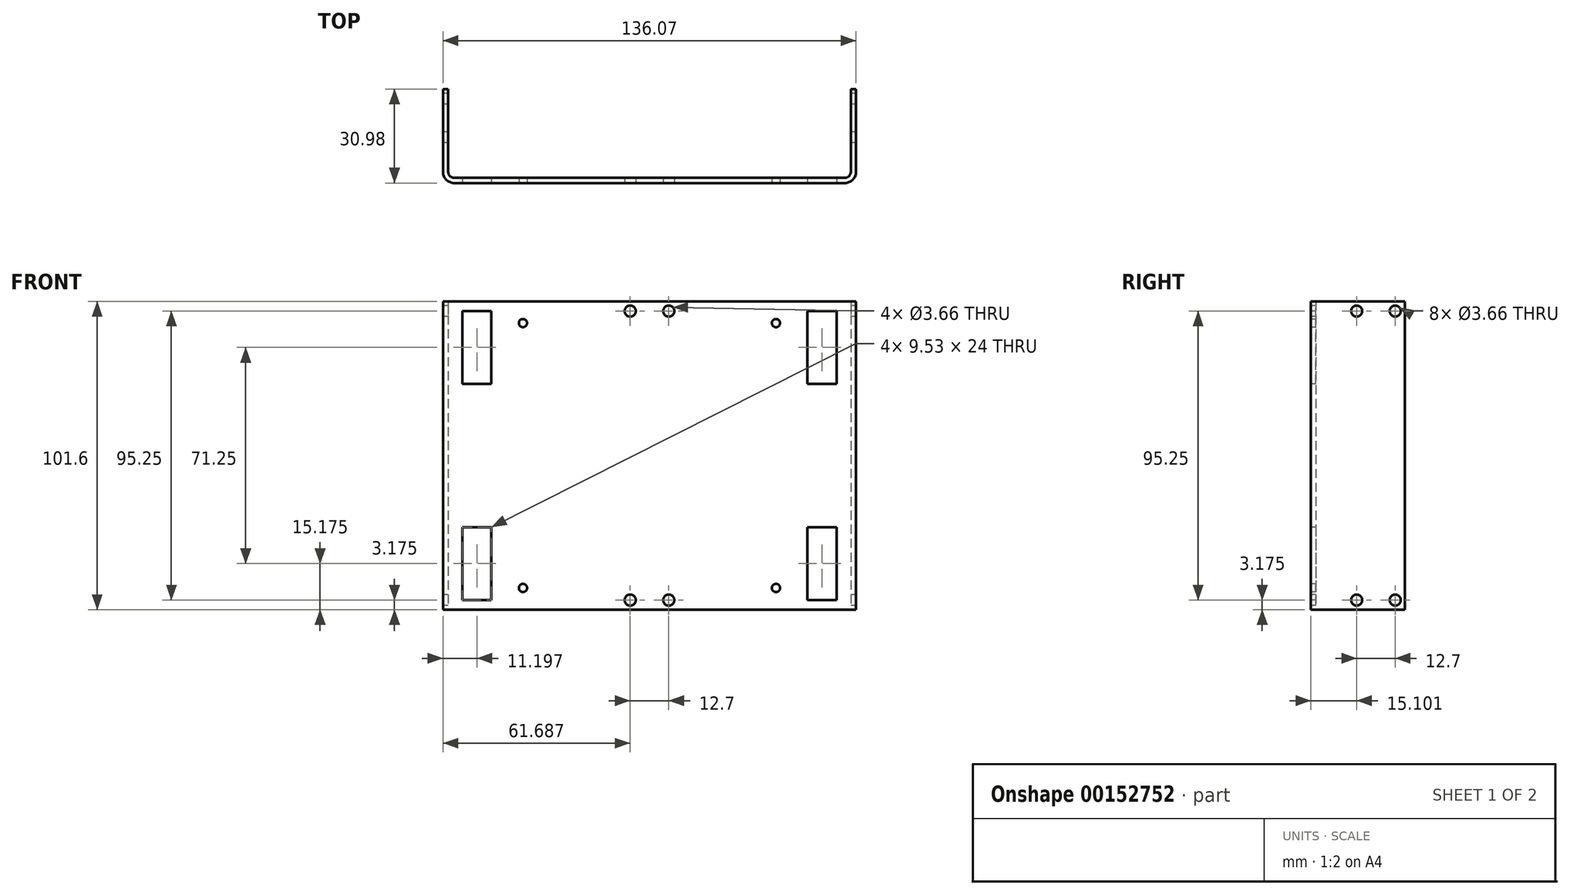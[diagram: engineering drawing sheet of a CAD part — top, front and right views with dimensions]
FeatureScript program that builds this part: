
annotation { "Feature Type Name" : "Feature", "Feature Type Description" : "" }
export const myFeature = defineFeature(function(context is Context, id is Id, definition is map)
    precondition{}
    {
        {
            var Q0;
            Q0=qCreatedBy(makeId("Top.planeOp"),FACE);
            var sketch = newSketch(context, id + "F0", { "sketchPlane" : qUnion([Q0])});
            skLineSegment(sketch, "E0.bottom", {"start": v(0, 0) * mm, "end": v(-132.65, 0) * mm});
            skLineSegment(sketch, "E0.top", {"start": v(1.7, -1.7) * mm, "end": v(-134.36, -1.7) * mm});
            skLineSegment(sketch, "E1.top", {"start": v(-132.65, 29.27) * mm, "end": v(-134.36, 29.27) * mm});
            skLineSegment(sketch, "E1.left", {"start": v(-132.65, 0) * mm, "end": v(-132.65, 29.27) * mm});
            skLineSegment(sketch, "E1.right", {"start": v(-134.36, -1.7) * mm, "end": v(-134.36, 29.27) * mm});
            skLineSegment(sketch, "E2.top", {"start": v(0, 29.27) * mm, "end": v(1.7, 29.27) * mm});
            skLineSegment(sketch, "E2.left", {"start": v(0, 0) * mm, "end": v(0, 29.27) * mm});
            skLineSegment(sketch, "E2.right", {"start": v(1.7, -1.7) * mm, "end": v(1.7, 29.27) * mm});
            skLineSegment(sketch, "E3", {"start": v(-66.32, 0) * mm, "end": v(-66.32, -1.7) * mm, "construction": true});
            skSolve(sketch);
        }
        {
            var Q0;
            Q0=qSketchRegion(id+"F0",true);
            extrude(context, id + "F1", {"entities" : qUnion([Q0]), "depth" : 101.6 * mm});
        }
        {
            var Q0;
            Q0=makeQuery(id+"FBItojHO8814Spz_1.opExtrude","CAP_EDGE",EDGE,{"disambiguationData":[OSD([sQuery(id+"FUP6qXxoG76JSYb_1.wireOp",EDGE,"THhbgtQy-TwxC-mwnz-G1VQ-umnQbeZaK48w.top")])],"isStart":true});
            var Q1;
            Q1=makeQuery(id+"FcdIcV9w6YY9zah_1.opExtrude","CAP_EDGE",EDGE,{"disambiguationData":[OSD([sQuery(id+"FU7sgaIbCbRhSfr_1.wireOp",EDGE,"F29Sxc5V-O2cl-wjtz-gx5o-reTTBG7m1pNU.top")])],"isStart":true});
            var Q2;
            Q2=makeQuery(id+"FxyfTe7Czhdyx7B_1.opExtrude","CAP_EDGE",EDGE,{"disambiguationData":[OSD([sQuery(id+"FSFcS7Rq7llt4xF_1.wireOp",EDGE,"t1tKkxU0-9nQq-L00X-xvmB-zDJKT8Ek5K4t.top")])],"isStart":true});
            var Q3;
            Q3=makeQuery(id+"FxyfTe7Czhdyx7B_1.opExtrude","CAP_EDGE",EDGE,{"disambiguationData":[OSD([sQuery(id+"FSFcS7Rq7llt4xF_1.wireOp",EDGE,"hRkMf9XR-YJFt-15pq-nWkK-FIu6sRtvibO9.top")])],"isStart":true});
            var Q4;
            Q4=makeQuery(id+"FcdIcV9w6YY9zah_1.opExtrude","CAP_EDGE",EDGE,{"disambiguationData":[OSD([sQuery(id+"FU7sgaIbCbRhSfr_1.wireOp",EDGE,"yv2bQU74-Eht6-uYuo-WBF2-3C4kyuaz0slr.top")])],"isStart":true});
            var Q5;
            Q5=makeQuery(id+"FBItojHO8814Spz_1.opExtrude","CAP_EDGE",EDGE,{"disambiguationData":[OSD([sQuery(id+"FUP6qXxoG76JSYb_1.wireOp",EDGE,"IUdUpv5F-JSBg-2lHB-rE6Q-IiAhZBjA2grY.top")])],"isStart":true});
            var Q6;
            Q6=makeQuery(id+"F1.opExtrude","SWEPT_EDGE",EDGE,{"disambiguationData":[OSD([sQuery(id+"F0.wireOp",EDGE,"E0.bottom"),sQuery(id+"F0.wireOp",EDGE,"E2.left")])]});
            var Q7;
            Q7=makeQuery(id+"F1.opExtrude","SWEPT_EDGE",EDGE,{"disambiguationData":[OSD([sQuery(id+"F0.wireOp",EDGE,"E0.bottom"),sQuery(id+"F0.wireOp",EDGE,"E1.left")])]});
            fillet(context, id + "F2", {"entities" : qUnion([Q0, Q1, Q2, Q3, Q4, Q5, Q6, Q7]), "radius" : 1.98 * mm, "tangentPropagation" : true, "allowEdgeOverflow" : false});
        }
        {
            var Q0;
            Q0=makeQuery(id+"F1.opExtrude","SWEPT_EDGE",EDGE,{"disambiguationData":[OSD([sQuery(id+"F0.wireOp",EDGE,"E0.top"),sQuery(id+"F0.wireOp",EDGE,"E1.right")])]});
            var Q1;
            Q1=makeQuery(id+"F1.opExtrude","SWEPT_EDGE",EDGE,{"disambiguationData":[OSD([sQuery(id+"F0.wireOp",EDGE,"E0.top"),sQuery(id+"F0.wireOp",EDGE,"E2.right")])]});
            fillet(context, id + "F3", {"entities" : qUnion([Q0, Q1]), "radius" : 3.7 * mm, "tangentPropagation" : true, "allowEdgeOverflow" : false});
        }
        {
            var Q0;
            Q0=makeQuery(id+"F2kHonbXZaQoFrR_1.boolean.opBoolean","MERGE",FACE,{"derivedFrom":[makeQuery(id+"FkwQQH4eT4IjhdK_1.boolean.opBoolean","MERGE",FACE,{"derivedFrom":[makeQuery(id+"F1.opExtrude","SWEPT_FACE",FACE,{"disambiguationData":[OSD([sQuery(id+"F0.wireOp",EDGE,"E0.top")])]}),makeQuery(id+"FkwQQH4eT4IjhdK_1.opExtrude","SWEPT_FACE",FACE,{"disambiguationData":[OSD([sQuery(id+"FvDFSbhwMPyTNrQ_1.wireOp",EDGE,"223FG13h-YrEq-unoX-9EOi-DwKLLmwbrteD.top")])]})]}),makeQuery(id+"F2kHonbXZaQoFrR_1.opExtrude","SWEPT_FACE",FACE,{"disambiguationData":[OSD([sQuery(id+"FsAbJG8AZOSwdHE_1.wireOp",EDGE,"WRaIy3id-o2EU-qHqw-IwdC-eHQZRSiK4KpF.bottom")])]})]});
            var sketch = newSketch(context, id + "F4", { "sketchPlane" : qUnion([Q0])});
            skLineSegment(sketch, "E4.bottom", {"start": v(-4.72, 3.18) * mm, "end": v(-14.25, 3.18) * mm});
            skLineSegment(sketch, "E4.top", {"start": v(-4.72, 27.18) * mm, "end": v(-14.25, 27.18) * mm});
            skLineSegment(sketch, "E4.left", {"start": v(-4.72, 3.18) * mm, "end": v(-4.72, 27.18) * mm});
            skLineSegment(sketch, "E4.right", {"start": v(-14.25, 3.18) * mm, "end": v(-14.25, 27.18) * mm});
            skLineSegment(sketch, "E5.bottom", {"start": v(-127.93, 3.18) * mm, "end": v(-118.4, 3.18) * mm});
            skLineSegment(sketch, "E5.top", {"start": v(-127.93, 27.18) * mm, "end": v(-118.4, 27.18) * mm});
            skLineSegment(sketch, "E5.left", {"start": v(-127.93, 3.18) * mm, "end": v(-127.93, 27.18) * mm});
            skLineSegment(sketch, "E5.right", {"start": v(-118.4, 3.18) * mm, "end": v(-118.4, 27.18) * mm});
            skLineSegment(sketch, "E6.bottom", {"start": v(-127.93, 98.43) * mm, "end": v(-118.4, 98.43) * mm});
            skLineSegment(sketch, "E6.top", {"start": v(-127.93, 74.42) * mm, "end": v(-118.4, 74.42) * mm});
            skLineSegment(sketch, "E6.left", {"start": v(-127.93, 98.43) * mm, "end": v(-127.93, 74.43) * mm});
            skLineSegment(sketch, "E6.right", {"start": v(-118.4, 98.43) * mm, "end": v(-118.4, 74.43) * mm});
            skLineSegment(sketch, "E7.bottom", {"start": v(-4.72, 98.43) * mm, "end": v(-14.25, 98.43) * mm});
            skLineSegment(sketch, "E7.top", {"start": v(-4.72, 74.42) * mm, "end": v(-14.25, 74.42) * mm});
            skLineSegment(sketch, "E7.left", {"start": v(-4.72, 98.43) * mm, "end": v(-4.72, 74.43) * mm});
            skLineSegment(sketch, "E7.right", {"start": v(-14.25, 98.43) * mm, "end": v(-14.25, 74.43) * mm});
            skLineSegment(sketch, "E8", {"start": v(-66.32, 0) * mm, "end": v(-66.32, 101.6) * mm, "construction": true});
            skLineSegment(sketch, "E9.bottom", {"start": v(-14.25, 27.18) * mm, "end": v(-118.4, 27.18) * mm, "construction": true});
            skLineSegment(sketch, "E9.top", {"start": v(-14.25, 74.42) * mm, "end": v(-118.4, 74.42) * mm, "construction": true});
            skLineSegment(sketch, "E9.left", {"start": v(-14.25, 27.18) * mm, "end": v(-14.25, 74.43) * mm, "construction": true});
            skLineSegment(sketch, "E9.right", {"start": v(-118.4, 27.18) * mm, "end": v(-118.4, 74.43) * mm, "construction": true});
            skPoint(sketch, "E9.middle", {"position": v(-66.32, 50.8) * mm});
            skLineSegment(sketch, "E10", {"start": v(-9.48, 27.18) * mm, "end": v(-9.48, 50.8) * mm, "construction": true});
            skLineSegment(sketch, "E11", {"start": v(-9.48, 50.8) * mm, "end": v(-1.98, 50.8) * mm, "construction": true});
            skLineSegment(sketch, "E12", {"start": v(-9.48, 3.18) * mm, "end": v(-9.48, 0) * mm, "construction": true});
            skLineSegment(sketch, "E13.bottom", {"start": v(-24.65, 7.14) * mm, "end": v(-108, 7.14) * mm, "construction": true});
            skLineSegment(sketch, "E13.top", {"start": v(-24.65, 94.46) * mm, "end": v(-108, 94.46) * mm, "construction": true});
            skLineSegment(sketch, "E13.left", {"start": v(-24.65, 7.14) * mm, "end": v(-24.65, 94.46) * mm, "construction": true});
            skLineSegment(sketch, "E13.right", {"start": v(-108, 7.14) * mm, "end": v(-108, 94.46) * mm, "construction": true});
            skLineSegment(sketch, "E14", {"start": v(-24.65, 7.14) * mm, "end": v(-24.65, 3.18) * mm, "construction": true});
            skLineSegment(sketch, "E15", {"start": v(-24.65, 3.18) * mm, "end": v(-14.25, 3.18) * mm, "construction": true});
            skCircle(sketch, "E16", {"center": v(-24.65, 7.14) * mm, "radius": 1.35 * mm});
            skCircle(sketch, "E17", {"center": v(-108, 7.14) * mm, "radius": 1.35 * mm});
            skCircle(sketch, "E18", {"center": v(-108, 94.46) * mm, "radius": 1.35 * mm});
            skCircle(sketch, "E19", {"center": v(-24.65, 94.46) * mm, "radius": 1.35 * mm});
            skPoint(sketch, "E20", {"position": v(-123.16, 3.18) * mm});
            skLineSegment(sketch, "E21.bottom", {"start": v(-59.97, 3.18) * mm, "end": v(-72.67, 3.18) * mm, "construction": true});
            skLineSegment(sketch, "E21.top", {"start": v(-59.97, 98.43) * mm, "end": v(-72.67, 98.43) * mm, "construction": true});
            skLineSegment(sketch, "E21.left", {"start": v(-59.97, 3.17) * mm, "end": v(-59.97, 98.43) * mm, "construction": true});
            skLineSegment(sketch, "E21.right", {"start": v(-72.67, 3.17) * mm, "end": v(-72.67, 98.43) * mm, "construction": true});
            skCircle(sketch, "E22", {"center": v(-59.97, 3.18) * mm, "radius": 1.83 * mm});
            skCircle(sketch, "E23", {"center": v(-72.67, 3.18) * mm, "radius": 1.83 * mm});
            skCircle(sketch, "E24", {"center": v(-59.97, 98.43) * mm, "radius": 1.83 * mm});
            skCircle(sketch, "E25", {"center": v(-72.67, 98.43) * mm, "radius": 1.83 * mm});
            skSolve(sketch);
        }
        {
            var Q0;
            Q0=qSketchRegion(id+"F4",true);
            var Q1;
            Q1=makeQuery(id+"F2kHonbXZaQoFrR_1.boolean.opBoolean","MERGE",FACE,{"derivedFrom":[makeQuery(id+"FkwQQH4eT4IjhdK_1.boolean.opBoolean","MERGE",FACE,{"derivedFrom":[makeQuery(id+"F1.opExtrude","SWEPT_FACE",FACE,{"disambiguationData":[OSD([sQuery(id+"F0.wireOp",EDGE,"E0.bottom")])]}),makeQuery(id+"FkwQQH4eT4IjhdK_1.opExtrude","SWEPT_FACE",FACE,{"disambiguationData":[OSD([sQuery(id+"FvDFSbhwMPyTNrQ_1.wireOp",EDGE,"223FG13h-YrEq-unoX-9EOi-DwKLLmwbrteD.bottom")])]})]}),makeQuery(id+"F2kHonbXZaQoFrR_1.opExtrude","SWEPT_FACE",FACE,{"disambiguationData":[OSD([sQuery(id+"FsAbJG8AZOSwdHE_1.wireOp",EDGE,"WRaIy3id-o2EU-qHqw-IwdC-eHQZRSiK4KpF.top")])]})]});
            extrude(context, id + "F5", {"entities" : qUnion([Q0]), "operationType" : NewBodyOperationType.REMOVE, "endBound" : BoundingType.UP_TO_SURFACE, "oppositeDirection" : true, "endBoundEntityFace" : qUnion([Q1]), "depth" : 25.4 * mm});
        }
        {
            var Q0;
            Q0=makeQuery(id+"F1.opExtrude","SWEPT_FACE",FACE,{"disambiguationData":[OSD([sQuery(id+"F0.wireOp",EDGE,"E1.right")])]});
            var sketch = newSketch(context, id + "F6", { "sketchPlane" : qUnion([Q0])});
            skLineSegment(sketch, "E26", {"start": v(-19.74, 0) * mm, "end": v(-19.74, 3.18) * mm, "construction": true});
            skLineSegment(sketch, "E27", {"start": v(-26.1, 3.18) * mm, "end": v(-13.4, 3.18) * mm, "construction": true});
            skLineSegment(sketch, "E28", {"start": v(-26.1, 3.18) * mm, "end": v(-29.27, 3.18) * mm, "construction": true});
            skLineSegment(sketch, "E29", {"start": v(-19.74, 101.6) * mm, "end": v(-19.74, 98.43) * mm, "construction": true});
            skLineSegment(sketch, "E30", {"start": v(-26.1, 98.43) * mm, "end": v(-13.4, 98.43) * mm, "construction": true});
            skCircle(sketch, "E31", {"center": v(-26.1, 3.18) * mm, "radius": 1.83 * mm});
            skCircle(sketch, "E32", {"center": v(-13.4, 3.18) * mm, "radius": 1.83 * mm});
            skCircle(sketch, "E33", {"center": v(-13.4, 98.43) * mm, "radius": 1.83 * mm});
            skCircle(sketch, "E34", {"center": v(-26.1, 98.43) * mm, "radius": 1.83 * mm});
            skSolve(sketch);
        }
        {
            var Q0;
            Q0 = qSketchRegion(id + "F6", true);
            var Q1;
            Q1=makeQuery(id+"F1.opExtrude","SWEPT_FACE",FACE,{"disambiguationData":[OSD([sQuery(id+"F0.wireOp",EDGE,"E2.right")])]});
            extrude(context, id + "F7", {"entities" : qUnion([Q0]), "operationType" : NewBodyOperationType.REMOVE, "endBound" : BoundingType.UP_TO_SURFACE, "oppositeDirection" : true, "endBoundEntityFace" : qUnion([Q1]), "depth" : 25.4 * mm});
        }
    });
